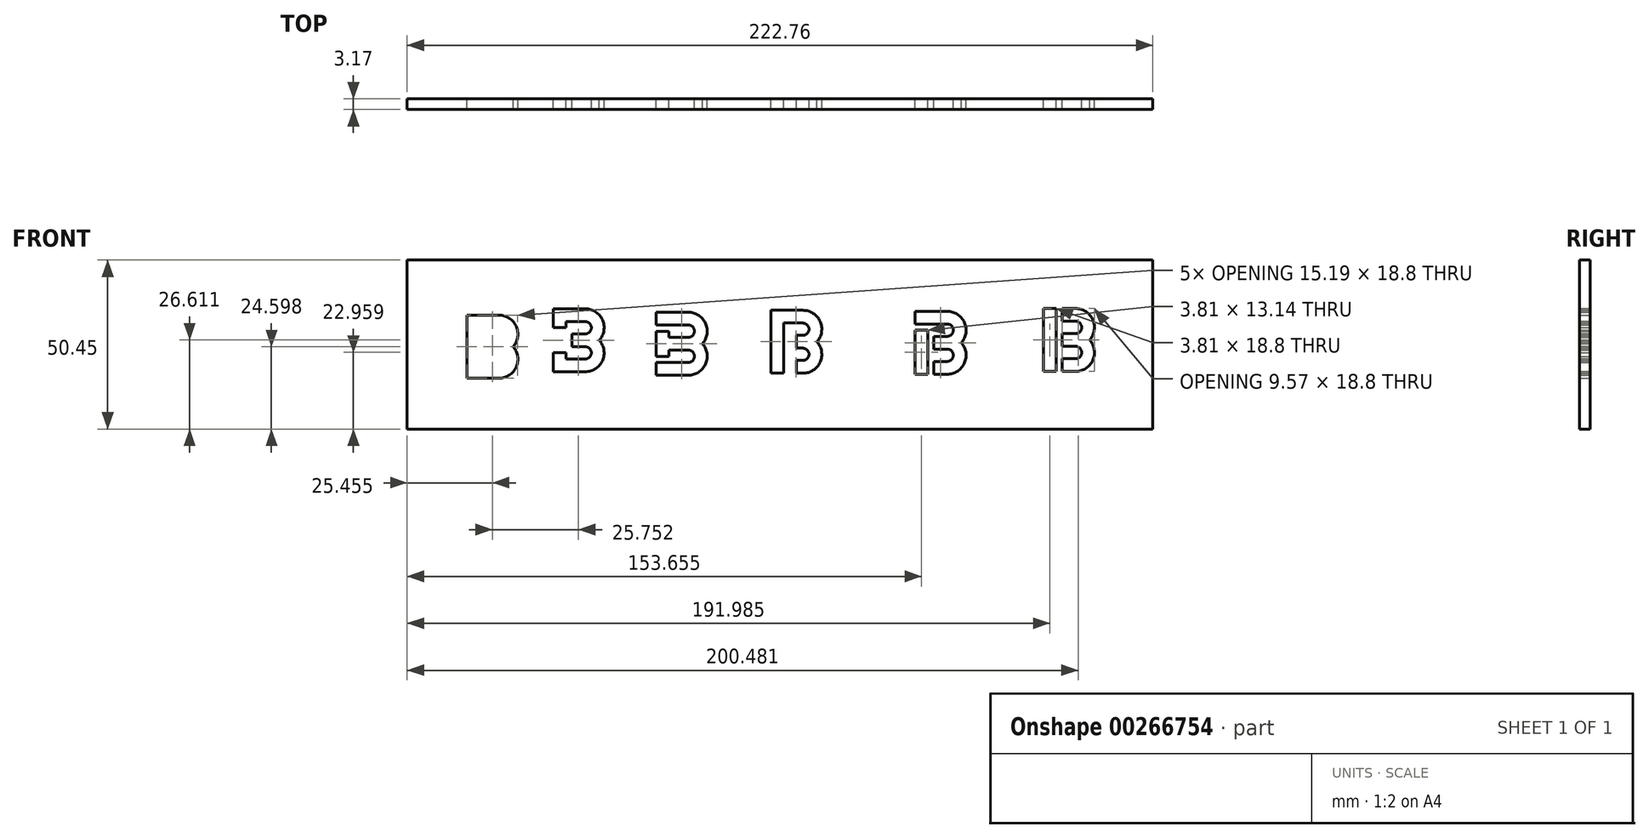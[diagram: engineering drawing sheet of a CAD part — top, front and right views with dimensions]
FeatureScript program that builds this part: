
annotation { "Feature Type Name" : "Feature", "Feature Type Description" : "" }
export const myFeature = defineFeature(function(context is Context, id is Id, definition is map)
    precondition{}
    {
        {
            var Q0;
            Q0=qCreatedBy(makeId("Front.planeOp"),FACE);
            var sketch = newSketch(context, id + "F0", { "sketchPlane" : qUnion([Q0])});
            skLineSegment(sketch, "E0", {"start": v(-72.54, 4.03) * mm, "end": v(-72.54, 22.83) * mm});
            skLineSegment(sketch, "E1", {"start": v(-72.54, 22.83) * mm, "end": v(-62.95, 22.83) * mm});
            skLineSegment(sketch, "E2", {"start": v(-72.54, 4.03) * mm, "end": v(-62.95, 4.03) * mm});
            skArc(sketch, "E3", {"start": v(-62.95, 4.03) * mm, "mid": v(-57.8, 7.36) * mm, "end": v(-58.72, 13.43) * mm});
            skArc(sketch, "E4", {"start": v(-58.72, 13.43) * mm, "mid": v(-57.8, 19.5) * mm, "end": v(-62.95, 22.83) * mm});
            skLineSegment(sketch, "E5", {"start": v(-62.95, 22.83) * mm, "end": v(-62.95, 22.83) * mm});
            skArc(sketch, "E6", {"start": v(-62.95, 15.33) * mm, "mid": v(-61.1, 17.17) * mm, "end": v(-62.95, 19.02) * mm});
            skArc(sketch, "E7", {"start": v(-62.95, 7.84) * mm, "mid": v(-61.1, 9.68) * mm, "end": v(-62.95, 11.52) * mm});
            skLineSegment(sketch, "E8.bottom", {"start": v(-62.95, 19.02) * mm, "end": v(-68.73, 19.02) * mm});
            skLineSegment(sketch, "E8.top", {"start": v(-62.95, 15.33) * mm, "end": v(-68.73, 15.33) * mm});
            skLineSegment(sketch, "E8.right", {"start": v(-68.73, 19.02) * mm, "end": v(-68.73, 15.33) * mm});
            skLineSegment(sketch, "E9.bottom", {"start": v(-62.95, 11.52) * mm, "end": v(-68.73, 11.52) * mm});
            skLineSegment(sketch, "E9.top", {"start": v(-62.95, 7.84) * mm, "end": v(-68.73, 7.84) * mm});
            skLineSegment(sketch, "E9.right", {"start": v(-68.73, 11.52) * mm, "end": v(-68.73, 7.84) * mm});
            skLineSegment(sketch, "E10", {"start": v(-46.79, 5.95) * mm, "end": v(-46.79, 11.6) * mm});
            skLineSegment(sketch, "E11", {"start": v(-46.79, 24.74) * mm, "end": v(-37.2, 24.74) * mm});
            skLineSegment(sketch, "E12", {"start": v(-46.79, 5.95) * mm, "end": v(-37.2, 5.95) * mm});
            skArc(sketch, "E13", {"start": v(-37.2, 5.95) * mm, "mid": v(-32.04, 9.28) * mm, "end": v(-32.97, 15.35) * mm});
            skArc(sketch, "E14", {"start": v(-32.97, 15.35) * mm, "mid": v(-32.04, 21.41) * mm, "end": v(-37.2, 24.74) * mm});
            skLineSegment(sketch, "E15", {"start": v(-37.2, 24.74) * mm, "end": v(-37.2, 24.74) * mm});
            skArc(sketch, "E16", {"start": v(-37.2, 17.25) * mm, "mid": v(-35.36, 19.1) * mm, "end": v(-37.2, 20.93) * mm});
            skArc(sketch, "E17", {"start": v(-37.2, 9.76) * mm, "mid": v(-35.36, 11.6) * mm, "end": v(-37.2, 13.44) * mm});
            skLineSegment(sketch, "E18.bottom", {"start": v(-37.2, 20.93) * mm, "end": v(-42.98, 20.93) * mm});
            skLineSegment(sketch, "E18.top", {"start": v(-37.2, 17.25) * mm, "end": v(-41.17, 17.25) * mm});
            skLineSegment(sketch, "E18.right", {"start": v(-42.98, 20.93) * mm, "end": v(-42.98, 19.1) * mm});
            skLineSegment(sketch, "E19.bottom", {"start": v(-37.2, 13.44) * mm, "end": v(-41.17, 13.44) * mm});
            skLineSegment(sketch, "E19.top", {"start": v(-37.2, 9.76) * mm, "end": v(-42.98, 9.76) * mm});
            skLineSegment(sketch, "E20", {"start": v(-15.99, 4.92) * mm, "end": v(-15.99, 8.73) * mm});
            skLineSegment(sketch, "E21", {"start": v(-15.99, 23.71) * mm, "end": v(-6.4, 23.71) * mm});
            skLineSegment(sketch, "E22", {"start": v(-15.99, 4.92) * mm, "end": v(-6.4, 4.92) * mm});
            skArc(sketch, "E23", {"start": v(-6.4, 4.92) * mm, "mid": v(-1.25, 8.25) * mm, "end": v(-2.17, 14.32) * mm});
            skArc(sketch, "E24", {"start": v(-2.17, 14.32) * mm, "mid": v(-1.25, 20.38) * mm, "end": v(-6.4, 23.71) * mm});
            skLineSegment(sketch, "E25", {"start": v(-14, 25.5) * mm, "end": v(-14, 25.5) * mm});
            skArc(sketch, "E26", {"start": v(-6.4, 16.22) * mm, "mid": v(-4.56, 18.06) * mm, "end": v(-6.4, 19.9) * mm});
            skArc(sketch, "E27", {"start": v(-6.4, 8.73) * mm, "mid": v(-4.56, 10.57) * mm, "end": v(-6.4, 12.41) * mm});
            skLineSegment(sketch, "E28.bottom", {"start": v(-6.4, 19.9) * mm, "end": v(-15.99, 19.9) * mm});
            skLineSegment(sketch, "E28.top", {"start": v(-6.4, 16.22) * mm, "end": v(-12.18, 16.22) * mm});
            skLineSegment(sketch, "E29.bottom", {"start": v(-6.4, 12.41) * mm, "end": v(-12.18, 12.41) * mm});
            skLineSegment(sketch, "E29.top", {"start": v(-6.4, 8.73) * mm, "end": v(-15.99, 8.73) * mm});
            skLineSegment(sketch, "E29.right", {"start": v(-12.18, 12.41) * mm, "end": v(-12.18, 10.57) * mm});
            skPoint(sketch, "E30.firstSnap0", {"position": v(-42.98, 19.1) * mm});
            skPoint(sketch, "E30.oppositeSnap0", {"position": v(-42.98, 11.6) * mm});
            skLineSegment(sketch, "E30.bottom", {"start": v(-46.79, 19.1) * mm, "end": v(-42.98, 19.1) * mm});
            skLineSegment(sketch, "E30.top", {"start": v(-46.79, 11.6) * mm, "end": v(-42.98, 11.6) * mm});
            skLineSegment(sketch, "E31", {"start": v(-42.98, 11.6) * mm, "end": v(-42.98, 9.76) * mm});
            skLineSegment(sketch, "E32", {"start": v(-41.17, 17.25) * mm, "end": v(-41.17, 13.44) * mm});
            skLineSegment(sketch, "E33", {"start": v(-46.79, 19.1) * mm, "end": v(-46.79, 24.74) * mm});
            skPoint(sketch, "E34.firstSnap0", {"position": v(-12.18, 18.06) * mm});
            skPoint(sketch, "E34.oppositeSnap0", {"position": v(-12.18, 10.57) * mm});
            skLineSegment(sketch, "E34.bottom", {"start": v(-15.99, 18.06) * mm, "end": v(-15.99, 18.06) * mm});
            skLineSegment(sketch, "E34.top", {"start": v(-15.99, 10.57) * mm, "end": v(-12.18, 10.57) * mm});
            skLineSegment(sketch, "E34.left", {"start": v(-15.99, 18.06) * mm, "end": v(-15.99, 10.57) * mm});
            skLineSegment(sketch, "E35", {"start": v(-15.99, 10.57) * mm, "end": v(-15.99, 18.06) * mm});
            skLineSegment(sketch, "E36", {"start": v(-12.18, 18.06) * mm, "end": v(-12.18, 16.22) * mm});
            skLineSegment(sketch, "E37", {"start": v(-15.99, 18.06) * mm, "end": v(-12.18, 18.06) * mm});
            skLineSegment(sketch, "E38", {"start": v(-15.99, 19.9) * mm, "end": v(-15.99, 23.71) * mm});
            skLineSegment(sketch, "E39", {"start": v(18.24, 5.5) * mm, "end": v(18.24, 24.3) * mm});
            skLineSegment(sketch, "E40", {"start": v(18.24, 24.3) * mm, "end": v(27.82, 24.3) * mm});
            skLineSegment(sketch, "E41", {"start": v(18.24, 5.5) * mm, "end": v(22.05, 5.5) * mm});
            skArc(sketch, "E42", {"start": v(27.82, 5.5) * mm, "mid": v(32.98, 8.83) * mm, "end": v(32.06, 14.9) * mm});
            skArc(sketch, "E43", {"start": v(32.06, 14.9) * mm, "mid": v(32.98, 20.96) * mm, "end": v(27.82, 24.3) * mm});
            skLineSegment(sketch, "E44", {"start": v(-14.6, 53.25) * mm, "end": v(-14.6, 53.25) * mm});
            skArc(sketch, "E45", {"start": v(27.82, 16.8) * mm, "mid": v(29.67, 18.64) * mm, "end": v(27.82, 20.48) * mm});
            skArc(sketch, "E46", {"start": v(27.82, 9.3) * mm, "mid": v(29.67, 11.15) * mm, "end": v(27.82, 13) * mm});
            skLineSegment(sketch, "E47.bottom", {"start": v(27.82, 20.48) * mm, "end": v(22.05, 20.48) * mm});
            skLineSegment(sketch, "E47.top", {"start": v(27.82, 16.8) * mm, "end": v(25.86, 16.8) * mm});
            skLineSegment(sketch, "E47.right", {"start": v(22.05, 20.48) * mm, "end": v(22.05, 5.5) * mm});
            skLineSegment(sketch, "E48.bottom", {"start": v(27.82, 13) * mm, "end": v(25.86, 13) * mm});
            skLineSegment(sketch, "E48.top", {"start": v(27.82, 9.3) * mm, "end": v(25.86, 9.3) * mm});
            skLineSegment(sketch, "E49", {"start": v(61.35, 5.22) * mm, "end": v(61.35, 18.36) * mm});
            skLineSegment(sketch, "E50", {"start": v(61.35, 24.01) * mm, "end": v(70.94, 24.01) * mm});
            skLineSegment(sketch, "E51", {"start": v(61.35, 5.22) * mm, "end": v(65.16, 5.22) * mm});
            skArc(sketch, "E52", {"start": v(70.94, 5.22) * mm, "mid": v(76.1, 8.55) * mm, "end": v(75.17, 14.61) * mm});
            skArc(sketch, "E53", {"start": v(75.17, 14.61) * mm, "mid": v(76.1, 20.68) * mm, "end": v(70.94, 24.01) * mm});
            skLineSegment(sketch, "E54", {"start": v(56.71, 39.5) * mm, "end": v(56.71, 39.5) * mm});
            skArc(sketch, "E55", {"start": v(70.94, 16.52) * mm, "mid": v(72.78, 18.36) * mm, "end": v(70.94, 20.2) * mm});
            skArc(sketch, "E56", {"start": v(70.94, 9.03) * mm, "mid": v(72.78, 10.87) * mm, "end": v(70.94, 12.7) * mm});
            skLineSegment(sketch, "E57.bottom", {"start": v(70.94, 20.2) * mm, "end": v(61.35, 20.2) * mm});
            skLineSegment(sketch, "E57.top", {"start": v(70.94, 16.52) * mm, "end": v(66.96, 16.52) * mm});
            skLineSegment(sketch, "E58.bottom", {"start": v(70.94, 12.7) * mm, "end": v(66.96, 12.7) * mm});
            skLineSegment(sketch, "E58.top", {"start": v(70.94, 9.03) * mm, "end": v(66.96, 9.03) * mm});
            skLineSegment(sketch, "E59", {"start": v(25.86, 16.8) * mm, "end": v(25.86, 13) * mm});
            skPoint(sketch, "E59.endSnap0", {"position": v(23.03, 5.5) * mm});
            skLineSegment(sketch, "E60", {"start": v(25.86, 9.3) * mm, "end": v(25.86, 5.5) * mm});
            skLineSegment(sketch, "E61", {"start": v(25.86, 5.5) * mm, "end": v(27.82, 5.5) * mm});
            skLineSegment(sketch, "E62", {"start": v(65.16, 18.36) * mm, "end": v(61.35, 18.36) * mm});
            skLineSegment(sketch, "E63", {"start": v(66.96, 16.52) * mm, "end": v(66.96, 12.7) * mm});
            skLineSegment(sketch, "E64", {"start": v(66.96, 9.03) * mm, "end": v(66.96, 5.22) * mm});
            skLineSegment(sketch, "E65", {"start": v(65.16, 18.36) * mm, "end": v(65.16, 5.22) * mm});
            skPoint(sketch, "E66.orphan", {"position": v(66.96, 8.96) * mm});
            skLineSegment(sketch, "E67.trimOffspring", {"start": v(66.96, 5.22) * mm, "end": v(70.94, 5.22) * mm});
            skLineSegment(sketch, "E68.trimOffspring", {"start": v(61.35, 20.2) * mm, "end": v(61.35, 24.01) * mm});
            skLineSegment(sketch, "E69", {"start": v(99.68, 6.04) * mm, "end": v(99.68, 24.84) * mm});
            skLineSegment(sketch, "E70", {"start": v(99.68, 24.84) * mm, "end": v(103.5, 24.84) * mm});
            skLineSegment(sketch, "E71", {"start": v(99.68, 6.04) * mm, "end": v(103.5, 6.04) * mm});
            skArc(sketch, "E72", {"start": v(109.27, 6.04) * mm, "mid": v(114.42, 9.37) * mm, "end": v(113.5, 15.44) * mm});
            skArc(sketch, "E73", {"start": v(113.5, 15.44) * mm, "mid": v(114.42, 21.5) * mm, "end": v(109.27, 24.84) * mm});
            skLineSegment(sketch, "E74", {"start": v(102.16, 34.5) * mm, "end": v(102.16, 34.5) * mm});
            skArc(sketch, "E75", {"start": v(109.27, 17.35) * mm, "mid": v(111.11, 19.19) * mm, "end": v(109.27, 21.03) * mm});
            skArc(sketch, "E76", {"start": v(109.27, 9.85) * mm, "mid": v(111.11, 11.7) * mm, "end": v(109.27, 13.54) * mm});
            skLineSegment(sketch, "E77.bottom", {"start": v(109.27, 21.03) * mm, "end": v(105.3, 21.03) * mm});
            skLineSegment(sketch, "E77.top", {"start": v(109.27, 17.35) * mm, "end": v(105.3, 17.35) * mm});
            skLineSegment(sketch, "E78.bottom", {"start": v(109.27, 13.54) * mm, "end": v(105.3, 13.54) * mm});
            skLineSegment(sketch, "E78.top", {"start": v(109.27, 9.85) * mm, "end": v(105.3, 9.85) * mm});
            skLineSegment(sketch, "E78.right", {"start": v(103.5, 24.84) * mm, "end": v(103.5, 6.04) * mm});
            skLineSegment(sketch, "E79", {"start": v(105.3, 6.04) * mm, "end": v(105.3, 9.85) * mm});
            skLineSegment(sketch, "E80.trimOffspring", {"start": v(105.3, 6.04) * mm, "end": v(109.27, 6.04) * mm});
            skLineSegment(sketch, "E81.trimOffspring", {"start": v(105.3, 24.84) * mm, "end": v(109.27, 24.84) * mm});
            skLineSegment(sketch, "E82.trimOffspring", {"start": v(105.3, 21.03) * mm, "end": v(105.3, 24.84) * mm});
            skLineSegment(sketch, "E83.trimOffspring", {"start": v(105.3, 13.54) * mm, "end": v(105.3, 17.35) * mm});
            skLineSegment(sketch, "E84.bottom", {"start": v(-90.4, 39.28) * mm, "end": v(132.36, 39.28) * mm});
            skLineSegment(sketch, "E84.top", {"start": v(-90.4, -11.17) * mm, "end": v(132.36, -11.17) * mm});
            skLineSegment(sketch, "E84.left", {"start": v(-90.4, 39.28) * mm, "end": v(-90.4, -11.17) * mm});
            skLineSegment(sketch, "E84.right", {"start": v(132.36, 39.28) * mm, "end": v(132.36, -11.17) * mm});
            skSolve(sketch);
        }
        {
            var Q0;
            Q0 = qSketchRegion(id + "F0", true);
            extrude(context, id + "F1", {"entities" : qUnion([Q0]), "depth" : 3.17 * mm});
        }
    });
